# Revit family: LHBC
name_source: partatom
category: Lighting Fixtures
units: mm (PartAtom-declared; Revit-internal decimal feet)

## family parameters
Cut with Voids When Loaded = No
Host = Face
Light Source = Yes
OmniClass Number = 23.80.70.11.14.11
OmniClass Title = Downlights
Part Type = Normal
Room Calculation Point = No
Round Connector Dimension = Use Diameter
Shared = No

## types (11) — shared parameters
Color Filter = 16777215
Default Elevation = 4' - 0"
Description = High Efficacy LED High Bay
Dimming Lamp Color Temperature Shift = <None>
Emit Shape Visible in Rendering = No
Housing Finish = Metal - Viscor - White
Lamp = LED
Manufacturer = VISIONEERING by VISCOR
Model = LHBC
Surface Ceiling = 0' - 0 3/16"
Tilt Angle = -90.00°
URL = https://www.viscor.com
Voltage = 120 V

## per-type parameters (varying)
| type | Apparent Load | Assembly Code | Emit from Rectangle Length | Emit from Rectangle Width | Lamp Wattage | Length | Photometric Web File | Width |
| LHBC224-LED840K120LUNV | 78 VA | D5020200 | 1' - 4" | 2' - 0" | 78 VA | 2' - 0" | LHBC224-LED840K120LUNV-G002339.IES | 1' - 4" |
| LHBC224-LED840K150LUNV | 102 VA |  | 1' - 4" | 2' - 0" | 102 VA | 2' - 0" | LHBC224-LED840K150LUNV-G002341.IES | 1' - 4" |
| LHBC248-LED840K240LUNV | 154 VA |  | 1' - 4" | 4' - 0" | 154 VA | 4' - 0" | LHBC248-LED840K240LUNV_G002372.IES | 1' - 4" |
| LHBC248-LED840K300LUNV | 203 VA |  | 1' - 4" | 4' - 0" | 203 VA | 4' - 0" | LHBC248-LED840K300LUNV_G002378.IES | 1' - 4" |
| LHBC424-LED840K180LUNV | 118 VA |  | 2' - 0" | 2' - 0" | 118 VA | 2' - 0" | LHBC424-LED840K180LUNV-G002347.IES | 2' - 0" |
| LHBC424-LED840K240LUNV | 154 VA |  | 2' - 0" | 2' - 0" | 154 VA | 2' - 0" | LHBC424-LED840K240LUNV_G002353.IES | 2' - 0" |
| LHBC424-LED840K300LUNV | 203 VA |  | 4' - 0" | 2' - 0" | 203 VA | 2' - 0" | LHBC424-LED840K300LUNV-G002359.IES | 2' - 0" |
| LHBC448-LED840K360LUNV | 234 VA |  | 2' - 0" | 4' - 0" | 234 VA | 4' - 0" | LHBC448-LED840K360LUNV_G002391.IES | 2' - 0" |
| LHBC448-LED840K420LUNV | 279 VA |  | 2' - 0" | 4' - 0" | 279 VA | 4' - 0" | LHBC448-LED840K420LUNV_G002385.IES | 2' - 0" |
| LHBC448-LED840K480LUNV | 312 VA |  | 2' - 0" | 4' - 0" | 312 VA | 4' - 0" | LHBC448-LED840K480LUNV-G002395.IES | 2' - 0" |
| LHBC448-LED840K600LUNV | 412 VA |  | 2' - 0" | 4' - 0" | 412 VA | 4' - 0" | LHBC448-LED840K600LUNV_G002399.IES | 2' - 0" |

## geometry (parser evidence)
native form markers: Sweep x3
no freeform markers — native parametric forms only
